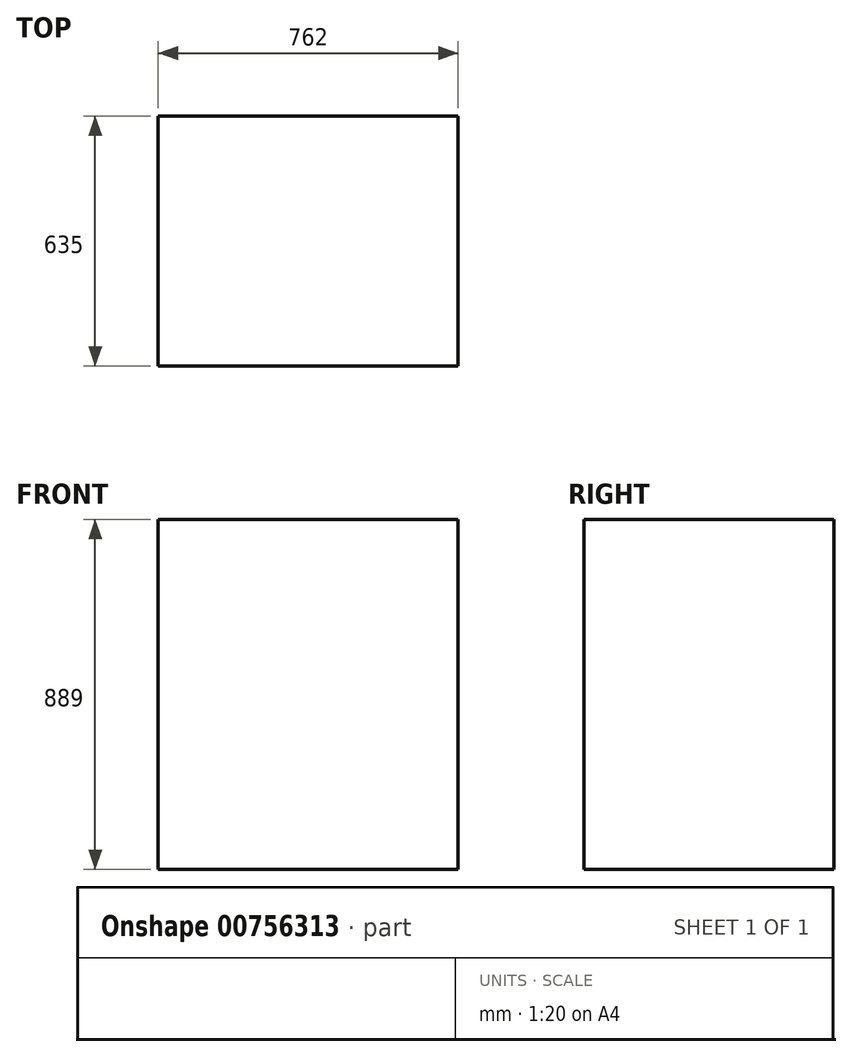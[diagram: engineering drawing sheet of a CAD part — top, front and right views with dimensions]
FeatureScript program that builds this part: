
annotation { "Feature Type Name" : "Feature", "Feature Type Description" : "" }
export const myFeature = defineFeature(function(context is Context, id is Id, definition is map)
    precondition{}
    {
        {
            var Q0;
            Q0=qCreatedBy(makeId("Top.planeOp"),FACE);
            var sketch = newSketch(context, id + "F0", { "sketchPlane" : qUnion([Q0])});
            skLineSegment(sketch, "E0.bottom", {"start": v(0, 0) * mm, "end": v(-762, 0) * mm});
            skLineSegment(sketch, "E0.top", {"start": v(0, 635) * mm, "end": v(-762, 635) * mm});
            skLineSegment(sketch, "E0.left", {"start": v(0, 0) * mm, "end": v(0, 635) * mm});
            skLineSegment(sketch, "E0.right", {"start": v(-762, 0) * mm, "end": v(-762, 635) * mm});
            skSolve(sketch);
        }
        {
            var Q0;
            Q0=makeQuery(id+"F0.imprint","IMPRINT",FACE,{"disambiguationData":[TD([[makeQuery(id+"F0.imprint","IMPRINT",EDGE,{"derivedFrom":sQuery(id+"F0.wireOp",EDGE,"E0.bottom")}),-1.0]])]});
            extrude(context, id + "F1", {"entities" : qUnion([Q0]), "oppositeDirection" : true, "depth" : 889 * mm, "offsetDistance" : 25.4 * mm});
        }
    });
